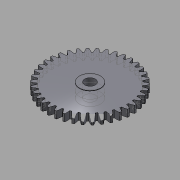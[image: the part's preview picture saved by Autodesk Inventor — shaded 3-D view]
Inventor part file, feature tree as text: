
AUTODESK INVENTOR PART (.ipt)
format: ipt  version: 2015 (Build 190159000, 159)  size: 299,520 bytes
history: native  units: mm (DEFAULTED — no unit token found)
features: sketch x5, extrude x4, plane x3, other x3
ambient origin geometry x8: Origin, YZ Plane, XZ Plane, XY Plane, X Axis, Y Axis, Z Axis, Center Point
bodies: Solid1 (feature_tree)
feature tree (15):
  extrude  "Extrusion1"  Depth=1.7mm TaperAngle=0.0deg
  plane  "Work Plane2"
  plane  "Work Plane8"
  plane  "Work Plane9"
  other  "Spur Gear"
  extrude  "Extrusion2"  Depth=10.0mm TaperAngle=0.0deg
  extrude  "Extrusion3"  Depth=0.826735mm TaperAngle=0.0deg
  extrude  "Extrusion4"  TaperAngle=0.0deg  [1 undecoded]
  sketch  "Sketch1"  dims[d0=20.0mm d1=1.7mm d2=0.0mm]
  sketch  "Sketch2"  dims[d3=19.0mm d4=10.0mm d5=0.0mm]
  other  "Srf1"
  sketch  "Sketch3"  dims[d16=14.5mm d17=0.0mm d34=0.826735mm]
  sketch  "Sketch4"  dims[d39=0.0mm d41=0.0mm]
  sketch  "Sketch5"  dims[d43=14.5mm d46=14.5mm d47=0.0mm d48=0.0mm d49=5.0mm d50=1.5mm d51=0.0mm d52=5.0mm d53=0.1mm d54=0.0mm d55=2.5mm d56=0.1mm d57=0.0mm]
  other  "Pitch Diameter"
note: 1 required parameter value undecoded (feature->parameter linkage not recoverable at this tier; creation-order binding heuristic only, values carry confidence <= 0.55)
